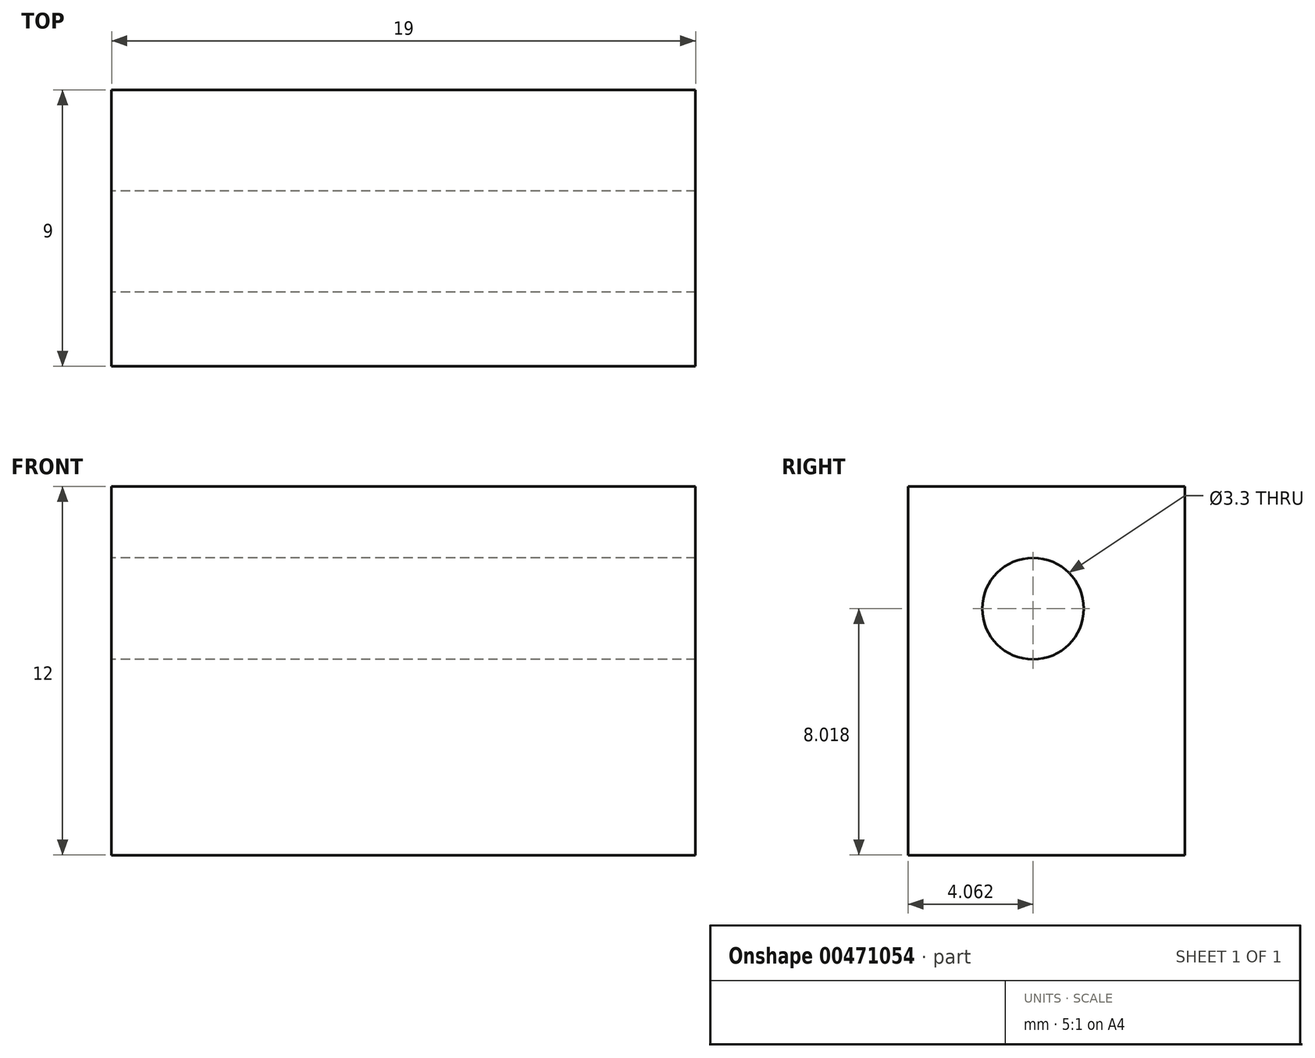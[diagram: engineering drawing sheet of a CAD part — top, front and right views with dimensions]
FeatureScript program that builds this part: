
annotation { "Feature Type Name" : "Feature", "Feature Type Description" : "" }
export const myFeature = defineFeature(function(context is Context, id is Id, definition is map)
    precondition{}
    {
        {
            var Q0;
            Q0=qCreatedBy(makeId("Front.planeOp"),FACE);
            var sketch = newSketch(context, id + "F0", { "sketchPlane" : qUnion([Q0])});
            skLineSegment(sketch, "E0.bottom", {"start": v(3.32, 32.9) * mm, "end": v(22.32, 32.9) * mm});
            skLineSegment(sketch, "E0.top", {"start": v(3.32, 20.9) * mm, "end": v(22.32, 20.9) * mm});
            skLineSegment(sketch, "E0.left", {"start": v(3.32, 32.9) * mm, "end": v(3.32, 20.9) * mm});
            skLineSegment(sketch, "E0.right", {"start": v(22.32, 32.9) * mm, "end": v(22.32, 20.9) * mm});
            skSolve(sketch);
        }
        {
            var Q0;
            Q0 = qSketchRegion(id + "F0", true);
            extrude(context, id + "F1", {"entities" : qUnion([Q0]), "depth" : 9 * mm, "offsetDistance" : 25 * mm});
        }
        {
            var Q0;
            Q0=qCreatedBy(makeId("Right.planeOp"),FACE);
            var sketch = newSketch(context, id + "F2", { "sketchPlane" : qUnion([Q0])});
            skCircle(sketch, "E1", {"center": v(-4.94, 28.92) * mm, "radius": 1.65 * mm});
            skSolve(sketch);
        }
        {
            var Q0;
            Q0=sQuery(id+"F2.wireOp",VERTEX,"E1.center");
            var Q1;
            Q1=makeQuery(id+"F1.opExtrude","SWEPT_BODY",BODY,{"disambiguationData":[OSD([sQuery(id+"F0.wireOp",EDGE,"E0.bottom"),sQuery(id+"F0.wireOp",EDGE,"E0.top"),sQuery(id+"F0.wireOp",EDGE,"E0.left"),sQuery(id+"F0.wireOp",EDGE,"E0.right")])]});
            hole(context, id + "F3", {"style" : HoleStyle.SIMPLE, "endStyle" : HoleEndStyle.THROUGH, "oppositeDirection" : true, "holeDiameter" : 3.3 * mm, "isTappedThrough" : true, "tappedDepth" : 12 * mm, "tapClearance" : 3, "locations" : qUnion([Q0]), "scope" : qUnion([Q1])});
        }
    });
